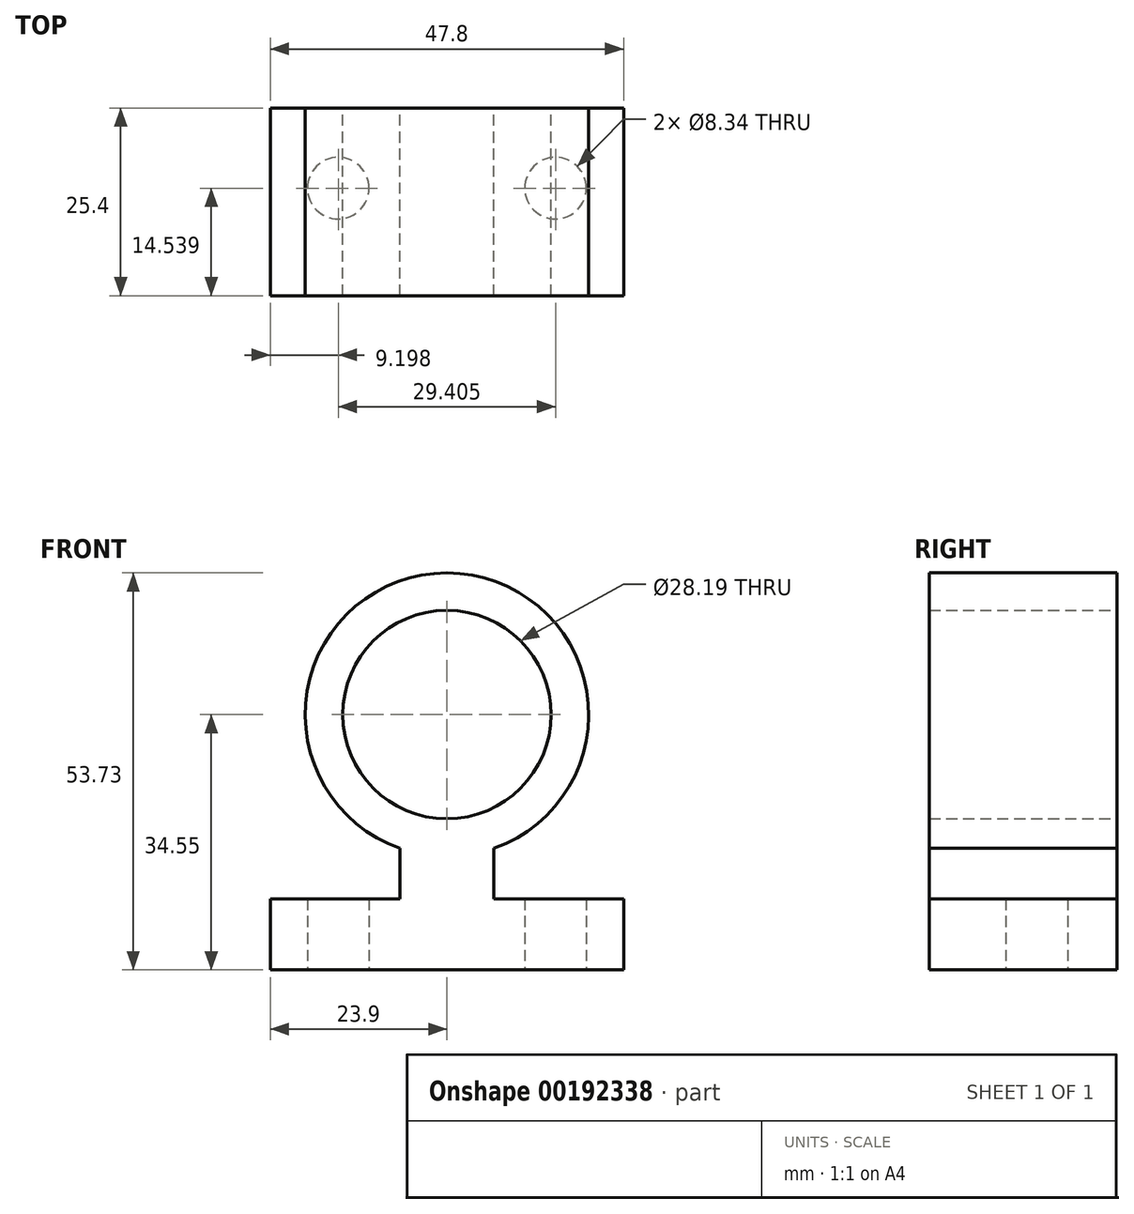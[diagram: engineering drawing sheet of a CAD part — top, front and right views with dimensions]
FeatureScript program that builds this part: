
annotation { "Feature Type Name" : "Feature", "Feature Type Description" : "" }
export const myFeature = defineFeature(function(context is Context, id is Id, definition is map)
    precondition{}
    {
        {
            var Q0;
            Q0=qCreatedBy(makeId("Front.planeOp"),FACE);
            var sketch = newSketch(context, id + "F0", { "sketchPlane" : qUnion([Q0])});
            skCircle(sketch, "E0", {"center": v(0, 0) * mm, "radius": 14.1 * mm});
            skArc(sketch, "E1", {"start": v(6.35, -18.1) * mm, "mid": v(0, 19.18) * mm, "end": v(-6.35, -18.1) * mm});
            skLineSegment(sketch, "E2", {"start": v(-19.18, 0) * mm, "end": v(-14.1, 0) * mm});
            skLineSegment(sketch, "E3.left", {"start": v(6.35, -24.93) * mm, "end": v(6.35, -18.1) * mm});
            skLineSegment(sketch, "E3.right", {"start": v(-6.35, -24.93) * mm, "end": v(-6.35, -18.1) * mm});
            skPoint(sketch, "E3.middle", {"position": v(0, -19.18) * mm});
            skPoint(sketch, "E4.orphan", {"position": v(6.35, -8.62) * mm});
            skPoint(sketch, "E5.trimOffspring.end.orphan", {"position": v(-6.35, -8.62) * mm});
            skLineSegment(sketch, "E6.bottom", {"start": v(23.9, -34.55) * mm, "end": v(-23.9, -34.55) * mm});
            skLineSegment(sketch, "E6.top", {"start": v(23.9, -24.93) * mm, "end": v(6.35, -24.93) * mm});
            skLineSegment(sketch, "E6.left", {"start": v(23.9, -34.55) * mm, "end": v(23.9, -24.93) * mm});
            skLineSegment(sketch, "E6.right", {"start": v(-23.9, -34.55) * mm, "end": v(-23.9, -24.93) * mm});
            skPoint(sketch, "E6.middle", {"position": v(0, -29.74) * mm});
            skPoint(sketch, "E7.orphan", {"position": v(-6.35, -29.74) * mm});
            skPoint(sketch, "E8.orphan", {"position": v(6.35, -29.74) * mm});
            skLineSegment(sketch, "E9.trimOffspring", {"start": v(-6.35, -24.93) * mm, "end": v(-23.9, -24.93) * mm});
            skSolve(sketch);
        }
        {
            var Q0;
            Q0=makeQuery(id+"F0.imprint","IMPRINT",FACE,{"disambiguationData":[TD([[makeQuery(id+"F0.imprint","IMPRINT",EDGE,{"derivedFrom":sQuery(id+"F0.wireOp",EDGE,"E0")}),-1.0]])]});
            var Q1;
            Q1 = qSketchRegion(id + "F2", true);
            extrude(context, id + "F1", {"entities" : qUnion([Q0, Q1]), "depth" : 25.4 * mm});
        }
        {
            var Q0;
            Q0=makeQuery(id+"F1.opExtrude","SWEPT_FACE",FACE,{"disambiguationData":[OSD([sQuery(id+"F0.wireOp",EDGE,"E6.bottom")])]});
            var sketch = newSketch(context, id + "F2", { "sketchPlane" : qUnion([Q0])});
            skCircle(sketch, "E10", {"center": v(-14.7, 10.86) * mm, "radius": 4.17 * mm});
            skCircle(sketch, "E11.MirrorC", {"center": v(14.7, 10.86) * mm, "radius": 4.17 * mm});
            skSolve(sketch);
        }
        {
            var Q0;
            Q0 = qSketchRegion(id + "F2", true);
            extrude(context, id + "F3", {"entities" : qUnion([Q0]), "operationType" : NewBodyOperationType.REMOVE, "oppositeDirection" : true, "depth" : 10.67 * mm});
        }
    });
